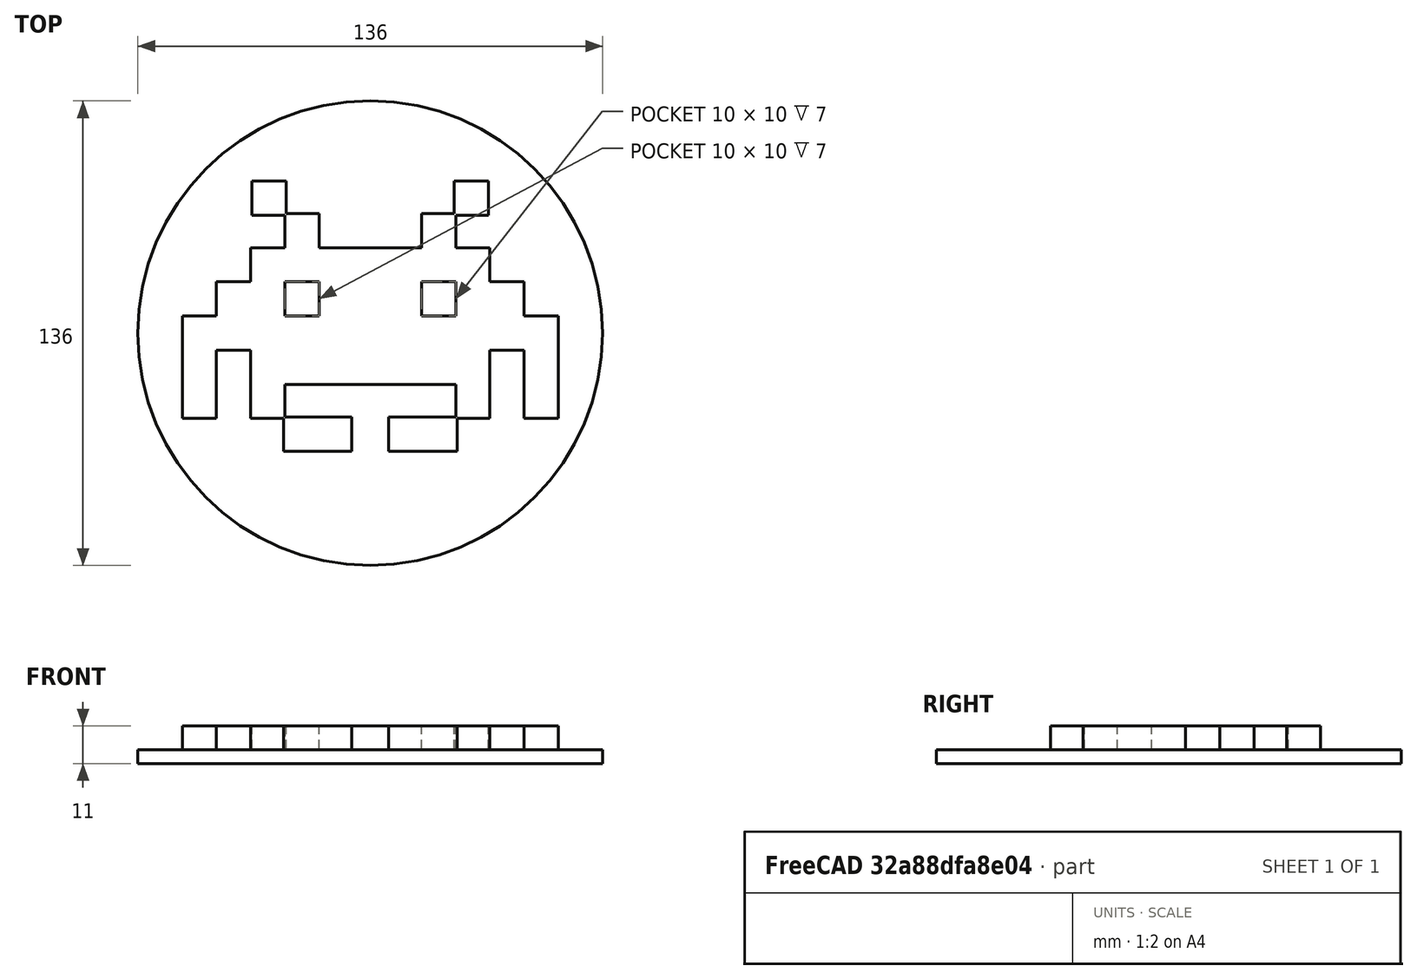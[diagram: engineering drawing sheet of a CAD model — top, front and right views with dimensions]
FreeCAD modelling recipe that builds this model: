
FCSTD DOCUMENT  (FreeCAD 0.16R6707 (Git))
Label: 09-invaders
License: All rights reserved
LicenseURL: http://en.wikipedia.org/wiki/All_rights_reserved
objects: Part::Box×25, Part::MultiFuse×3, Part::Cylinder×1, Part::Mirroring×1
note: 30 computed .brp shape members not serialized (recipe doc carries the construction recipe); baked Part::Feature solids carry a one-line shape summary decoded from their .brp

FEATURE [Part::Box] Box  label="Cubo"
  Height = 10
  Length = 10
  Placement = pos=(-35,15,0) rot=(0,0,1;0rad)
  Width = 10
FEATURE [Part::Box] Box001  label="Cubo001"
  Height = 10
  Length = 10
  Placement = pos=(-34.6,34.5,0) rot=(0,0,1;0rad)
  Width = 10
FEATURE [Part::Box] Box002  label="Cubo002"
  Height = 10
  Length = 10
  Placement = pos=(-25,25,0) rot=(0,0,1;0rad)
  Width = 10
FEATURE [Part::Box] Box003  label="Cubo003"
  Height = 10
  Length = 10
  Placement = pos=(-25,15,0) rot=(0,0,1;0rad)
  Width = 10
FEATURE [Part::Box] Box004  label="Cubo004"
  Height = 10
  Length = 10
  Placement = pos=(-15,15,0) rot=(0,0,1;0rad)
  Width = 10
FEATURE [Part::Box] Box005  label="Cubo005"
  Height = 10
  Length = 10
  Placement = pos=(-45,5,0) rot=(0,0,1;0rad)
  Width = 10
FEATURE [Part::Box] Box006  label="Cubo006"
  Height = 10
  Length = 10
  Placement = pos=(-35,5,0) rot=(0,0,1;0rad)
  Width = 10
FEATURE [Part::Box] Box007  label="Cubo007"
  Height = 10
  Length = 10
  Placement = pos=(-15,5,0) rot=(0,0,1;0rad)
  Width = 10
FEATURE [Part::Box] Box008  label="Cubo008"
  Height = 10
  Length = 10
  Placement = pos=(-55,-5,0) rot=(0,0,1;0rad)
  Width = 10
FEATURE [Part::Box] Box009  label="Cubo009"
  Height = 10
  Length = 10
  Placement = pos=(-45,-5,0) rot=(0,0,1;0rad)
  Width = 10
FEATURE [Part::Box] Box010  label="Cubo010"
  Height = 10
  Length = 10
  Placement = pos=(-35,-5,0) rot=(0,0,1;0rad)
  Width = 10
FEATURE [Part::Box] Box011  label="Cubo011"
  Height = 10
  Length = 10
  Placement = pos=(-25,-5,0) rot=(0,0,1;0rad)
  Width = 10
FEATURE [Part::Box] Box012  label="Cubo012"
  Height = 10
  Length = 10
  Placement = pos=(-15,-5,0) rot=(0,0,1;0rad)
  Width = 10
FEATURE [Part::Box] Box013  label="Cubo013"
  Height = 10
  Length = 10
  Placement = pos=(-55,-15,0) rot=(0,0,1;0rad)
  Width = 10
FEATURE [Part::Box] Box014  label="Cubo014"
  Height = 10
  Length = 10
  Placement = pos=(-55,-25,0) rot=(0,0,1;0rad)
  Width = 10
FEATURE [Part::Box] Box015  label="Cubo015"
  Height = 10
  Length = 10
  Placement = pos=(-35,-15,0) rot=(0,0,1;0rad)
  Width = 10
FEATURE [Part::Box] Box016  label="Cubo016"
  Height = 10
  Length = 10
  Placement = pos=(-35,-25,0) rot=(0,0,1;0rad)
  Width = 10
FEATURE [Part::Box] Box017  label="Cubo017"
  Height = 10
  Length = 10
  Placement = pos=(-25,-15,0) rot=(0,0,1;0rad)
  Width = 10
FEATURE [Part::Box] Box018  label="Cubo018"
  Height = 10
  Length = 10
  Placement = pos=(-15,-15,0) rot=(0,0,1;0rad)
  Width = 10
FEATURE [Part::Box] Box019  label="Cubo019"
  Height = 10
  Length = 10
  Placement = pos=(-25.4,-34.6,0) rot=(0,0,1;0rad)
  Width = 10
FEATURE [Part::Box] Box020  label="Cubo020"
  Height = 10
  Length = 10
  Placement = pos=(-15.4,-34.6,0) rot=(0,0,1;0rad)
  Width = 10
FEATURE [Part::Box] Box021  label="Cubo021"
  Height = 10
  Length = 10
  Placement = pos=(-5,15,0) rot=(0,0,1;0rad)
  Width = 10
FEATURE [Part::Box] Box022  label="Cubo022"
  Height = 10
  Length = 10
  Placement = pos=(-5,5,0) rot=(0,0,1;0rad)
  Width = 10
FEATURE [Part::Box] Box023  label="Cubo023"
  Height = 10
  Length = 10
  Placement = pos=(-5,-5,0) rot=(0,0,1;0rad)
  Width = 10
FEATURE [Part::Box] Box024  label="Cubo024"
  Height = 10
  Length = 10
  Placement = pos=(-5,-15,0) rot=(0,0,1;0rad)
  Width = 10
FEATURE [Part::Cylinder] Cylinder  label="Base"
  Angle = 360
  Height = 4
  Placement = pos=(0,0,-1) rot=(0,0,1;0rad)
  Radius = 68
FEATURE [Part::MultiFuse] Fusion  label="Lado-izdo"
  Shapes = -> [Box008,Box011,Box012,Box001,Box003,Box020,Box019,Box024,Box017,Box007,Box013,Box006,Box005,Box002,Box015,Box023,Box004,Box014,Box009,Box016,Box010,Box,Box022,Box018,Box021]
FEATURE [Part::Mirroring] Part__Mirroring  label="Lado-derecho"
  Base = (0,0,0)
  Normal = (1,0,0)
  Source = -> Fusion
FEATURE [Part::MultiFuse] Fusion001  label="Invaders"
  Shapes = -> [Part__Mirroring,Fusion]
FEATURE [Part::MultiFuse] Fusion002  label="Invaders-final"
  Shapes = -> [Cylinder,Fusion001]
